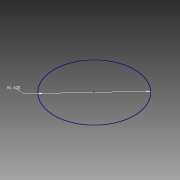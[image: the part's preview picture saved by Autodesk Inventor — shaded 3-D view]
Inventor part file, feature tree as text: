
AUTODESK INVENTOR PART (.ipt)
format: ipt  version: 2015 (Build 190159000, 159)  size: 59,392 bytes
history: native  units: in
note: dims shown in document units (in); Inventor stores cm internally (conversion verified against a paired STEP export)
features: sketch x1
ambient origin geometry x8: Origin, YZ Plane, XZ Plane, XY Plane, X Axis, Y Axis, Z Axis, Center Point
feature tree (1):
  sketch  "Sketch3"  dims[d4=0.625in]
